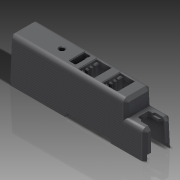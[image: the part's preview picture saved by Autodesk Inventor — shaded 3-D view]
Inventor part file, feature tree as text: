
AUTODESK INVENTOR PART (.ipt)
format: ipt  version: 2014 SP1 (Build 180222100, 222)  size: 964,608 bytes
history: native  units: in
note: dims shown in document units (in); Inventor stores cm internally (conversion verified against a paired STEP export)
features: fillet x1, imported_body x1
ambient origin geometry x8: Origin, YZ Plane, XZ Plane, XY Plane, X Axis, Y Axis, Z Axis, Center Point
bodies: Body1 (feature_tree)
feature tree (2):
  fillet  "Fillet16"  [1 undecoded]
  imported_body  "Base1"
note: 1 required parameter value undecoded (feature->parameter linkage not recoverable at this tier; creation-order binding heuristic only, values carry confidence <= 0.55)
